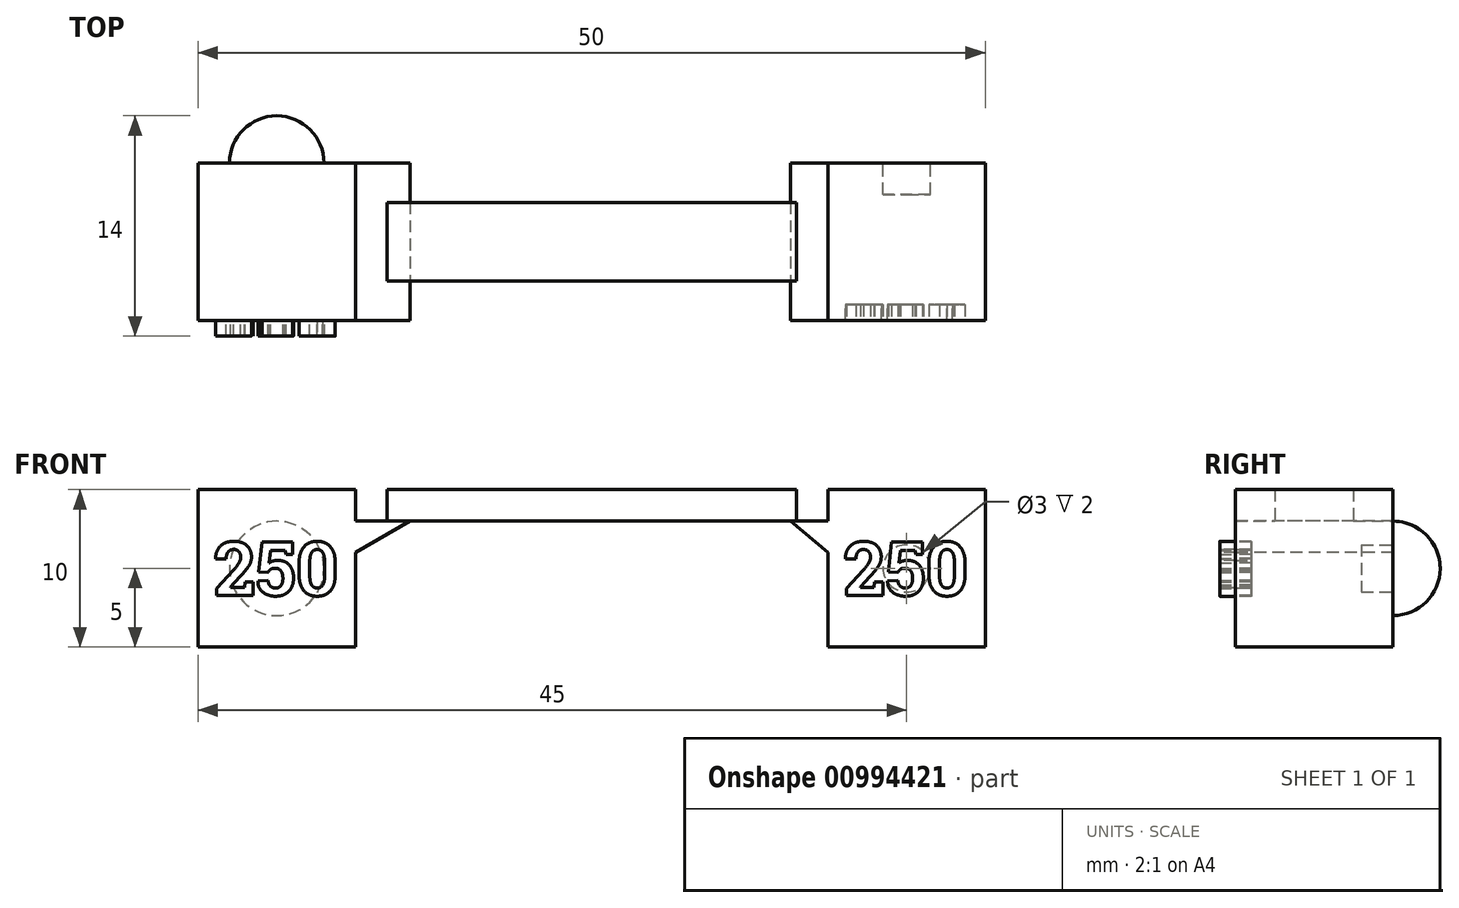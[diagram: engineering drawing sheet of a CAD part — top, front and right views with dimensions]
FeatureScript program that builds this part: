
annotation { "Feature Type Name" : "Feature", "Feature Type Description" : "" }
export const myFeature = defineFeature(function(context is Context, id is Id, definition is map)
    precondition{}
    {
        {
            var Q0;
            Q0=qCreatedBy(makeId("Top.planeOp"),FACE);
            var sketch = newSketch(context, id + "F0", { "sketchPlane" : qUnion([Q0])});
            skLineSegment(sketch, "E0.bottom", {"start": v(30, 10) * mm, "end": v(-30, 10) * mm});
            skLineSegment(sketch, "E0.top", {"start": v(30, -10) * mm, "end": v(-30, -10) * mm});
            skLineSegment(sketch, "E0.left", {"start": v(30, 10) * mm, "end": v(30, -10) * mm});
            skLineSegment(sketch, "E0.right", {"start": v(-30, 10) * mm, "end": v(-30, -10) * mm});
            skPoint(sketch, "E0.middle", {"position": v(0, 0) * mm});
            skLineSegment(sketch, "E1", {"start": v(0, 0) * mm, "end": v(-20, 0) * mm, "construction": true});
            skLineSegment(sketch, "E2.bottom", {"start": v(-15, 5) * mm, "end": v(-25, 5) * mm});
            skLineSegment(sketch, "E2.top", {"start": v(-15, -5) * mm, "end": v(-25, -5) * mm});
            skLineSegment(sketch, "E2.left", {"start": v(-15, 5) * mm, "end": v(-15, -5) * mm});
            skLineSegment(sketch, "E2.right", {"start": v(-25, 5) * mm, "end": v(-25, -5) * mm});
            skPoint(sketch, "E2.middle", {"position": v(-20, 0) * mm});
            skLineSegment(sketch, "E3", {"start": v(0, 0) * mm, "end": v(0, 4.45) * mm, "construction": true});
            skLineSegment(sketch, "E4.0", {"start": v(-16, 4) * mm, "end": v(-24, 4) * mm});
            skLineSegment(sketch, "E4.1", {"start": v(-16, 4) * mm, "end": v(-16, -4) * mm});
            skLineSegment(sketch, "E4.2", {"start": v(-16, -4) * mm, "end": v(-24, -4) * mm});
            skLineSegment(sketch, "E4.3", {"start": v(-24, 4) * mm, "end": v(-24, -4) * mm});
            skLineSegment(sketch, "E5.MirrorCS", {"start": v(-16, -4) * mm, "end": v(-16, 4) * mm});
            skLineSegment(sketch, "E6.MirrorCS", {"start": v(-25, -5) * mm, "end": v(-25, 5) * mm});
            skLineSegment(sketch, "E7.MirrorCS", {"start": v(-15, -5) * mm, "end": v(-15, 5) * mm});
            skLineSegment(sketch, "E8.MirrorCS", {"start": v(-24, -4) * mm, "end": v(-24, 4) * mm});
            skPoint(sketch, "E9.MirrorP", {"position": v(20, 0) * mm});
            skLineSegment(sketch, "E10.MirrorCS", {"start": v(25, 5) * mm, "end": v(25, -5) * mm});
            skLineSegment(sketch, "E11.MirrorCS", {"start": v(16, -4) * mm, "end": v(16, 4) * mm});
            skLineSegment(sketch, "E12.MirrorCS", {"start": v(15, -5) * mm, "end": v(25, -5) * mm});
            skLineSegment(sketch, "E13.MirrorCS", {"start": v(15, 5) * mm, "end": v(15, -5) * mm});
            skLineSegment(sketch, "E14.MirrorCS", {"start": v(16, -4) * mm, "end": v(24, -4) * mm});
            skLineSegment(sketch, "E15.MirrorCS", {"start": v(24, -4) * mm, "end": v(24, 4) * mm});
            skLineSegment(sketch, "E16.MirrorCS", {"start": v(15, 5) * mm, "end": v(25, 5) * mm});
            skLineSegment(sketch, "E17.MirrorCS", {"start": v(16, 4) * mm, "end": v(24, 4) * mm});
            skLineSegment(sketch, "E18.MirrorCS", {"start": v(16, 4) * mm, "end": v(16, -4) * mm});
            skLineSegment(sketch, "E19.MirrorCS", {"start": v(15, -5) * mm, "end": v(15, 5) * mm});
            skLineSegment(sketch, "E20.MirrorCS", {"start": v(24, 4) * mm, "end": v(24, -4) * mm});
            skLineSegment(sketch, "E21.MirrorCS", {"start": v(0, 0) * mm, "end": v(20, 0) * mm, "construction": true});
            skLineSegment(sketch, "E22.MirrorCS", {"start": v(25, -5) * mm, "end": v(25, 5) * mm});
            skLineSegment(sketch, "E23.bottom", {"start": v(15, 2.5) * mm, "end": v(-15, 2.5) * mm});
            skLineSegment(sketch, "E23.top", {"start": v(15, -2.5) * mm, "end": v(-15, -2.5) * mm});
            skLineSegment(sketch, "E23.left", {"start": v(15, 2.5) * mm, "end": v(15, -2.5) * mm});
            skLineSegment(sketch, "E23.right", {"start": v(-15, 2.5) * mm, "end": v(-15, -2.5) * mm});
            skSolve(sketch);
        }
        {
            var Q0;
            {var subQ4=sQuery(id+"F0.wireOp",EDGE,"E2.bottom");Q0=makeQuery(id+"F0.imprint","IMPRINT",FACE,{"disambiguationData":[TD([[makeQuery(id+"F0.imprint","IMPRINT",EDGE,{"derivedFrom":subQ4}),1.0]])]});}
            var Q1;
            Q1=makeQuery(id+"F0.imprint","IMPRINT",FACE,{"disambiguationData":[TD([[makeQuery(id+"F0.imprint","IMPRINT",EDGE,{"derivedFrom":sQuery(id+"F0.wireOp",EDGE,"E4.0")}),1.0]])]});
            var Q2;
            Q2=makeQuery(id+"F0.imprint","IMPRINT",FACE,{"disambiguationData":[TD([[makeQuery(id+"F0.imprint","IMPRINT",EDGE,{"derivedFrom":sQuery(id+"F0.wireOp",EDGE,"E11.MirrorCS")}),-1.0]])]});
            var Q3;
            Q3=makeQuery(id+"F0.imprint","IMPRINT",FACE,{"disambiguationData":[TD([[makeQuery(id+"F0.imprint","IMPRINT",EDGE,{"derivedFrom":sQuery(id+"F0.wireOp",EDGE,"E10.MirrorCS")}),-1.0]])]});
            var Q4;
            {var subQ0=sQuery(id+"F0.wireOp",EDGE,"E23.bottom");Q4=makeQuery(id+"F0.imprint","IMPRINT",FACE,{"disambiguationData":[TD([[makeQuery(id+"F0.imprint","IMPRINT",EDGE,{"derivedFrom":subQ0}),1.0]])]});}
            extrude(context, id + "F1", {"entities" : qUnion([Q0, Q1, Q2, Q3, Q4]), "depth" : 12 * mm, "offsetDistance" : 25 * mm, "hasSecondDirection" : true, "secondDirectionOppositeDirection" : false, "secondDirectionDepth" : 2 * mm});
        }
        {
            var Q0;
            Q0=makeQuery(id+"F1.opExtrude","SWEPT_FACE",FACE,{"disambiguationData":[OSD([sQuery(id+"F0.wireOp",EDGE,"E23.top")])]});
            var sketch = newSketch(context, id + "F2", { "sketchPlane" : qUnion([Q0])});
            skLineSegment(sketch, "E24.bottom", {"start": v(-15, 2) * mm, "end": v(15, 2) * mm});
            skLineSegment(sketch, "E24.top", {"start": v(-15, 8) * mm, "end": v(15, 8) * mm});
            skLineSegment(sketch, "E24.left", {"start": v(-15, 2) * mm, "end": v(-15, 8) * mm});
            skLineSegment(sketch, "E24.right", {"start": v(15, 2) * mm, "end": v(15, 8) * mm});
            skLineSegment(sketch, "E25.bottom", {"start": v(-13, 12) * mm, "end": v(13, 12) * mm});
            skLineSegment(sketch, "E25.top", {"start": v(-13, 10) * mm, "end": v(13, 10) * mm});
            skLineSegment(sketch, "E25.left", {"start": v(-13, 12) * mm, "end": v(-13, 10) * mm});
            skLineSegment(sketch, "E25.right", {"start": v(13, 12) * mm, "end": v(13, 10) * mm});
            skLineSegment(sketch, "E26", {"start": v(-15, 8) * mm, "end": v(-11.54, 10) * mm});
            skLineSegment(sketch, "E27", {"start": v(-11.54, 10) * mm, "end": v(-15, 10) * mm});
            skLineSegment(sketch, "E28", {"start": v(-15, 10) * mm, "end": v(-15, 8) * mm});
            skLineSegment(sketch, "E29", {"start": v(15, 8) * mm, "end": v(12.62, 10) * mm});
            skLineSegment(sketch, "E30", {"start": v(12.62, 10) * mm, "end": v(15, 10) * mm});
            skLineSegment(sketch, "E31", {"start": v(15, 10) * mm, "end": v(15, 8) * mm});
            skSolve(sketch);
        }
        {
            var Q0;
            Q0=makeQuery(id+"F2.imprint","IMPRINT",FACE,{"disambiguationData":[TD([[makeQuery(id+"F2.imprint","IMPRINT",EDGE,{"derivedFrom":sQuery(id+"F2.wireOp",EDGE,"E24.bottom")}),-1.0]])]});
            var Q1;
            Q1=makeQuery(id+"F2.imprint","IMPRINT",FACE,{"disambiguationData":[TD([[makeQuery(id+"F2.imprint","IMPRINT",EDGE,{"derivedFrom":sQuery(id+"F2.wireOp",EDGE,"E24.top")}),1.0]])]});
            var Q2;
            {var subQ0=sQuery(id+"F2.wireOp",EDGE,"E25.left");Q2=makeQuery(id+"F2.imprint","IMPRINT",FACE,{"disambiguationData":[TD([[makeQuery(id+"F2.imprint","IMPRINT",EDGE,{"derivedFrom":subQ0}),-1.0]])]});}
            var Q3;
            {var subQ0=sQuery(id+"F2.wireOp",EDGE,"E25.right");Q3=makeQuery(id+"F2.imprint","IMPRINT",FACE,{"disambiguationData":[TD([[makeQuery(id+"F2.imprint","IMPRINT",EDGE,{"derivedFrom":subQ0}),1.0]])]});}
            extrude(context, id + "F3", {"entities" : qUnion([Q0, Q1, Q2, Q3]), "operationType" : NewBodyOperationType.REMOVE, "oppositeDirection" : true, "depth" : 25 * mm, "offsetDistance" : 25 * mm});
        }
        {
            var Q0;
            {var subQ0=sQuery(id+"F2.wireOp",EDGE,"E26");Q0=makeQuery(id+"F2.imprint","IMPRINT",FACE,{"disambiguationData":[TD([[makeQuery(id+"F2.imprint","IMPRINT",EDGE,{"derivedFrom":subQ0}),1.0]])]});}
            var Q1;
            {var subQ0=sQuery(id+"F2.wireOp",EDGE,"E29");Q1=makeQuery(id+"F2.imprint","IMPRINT",FACE,{"disambiguationData":[TD([[makeQuery(id+"F2.imprint","IMPRINT",EDGE,{"derivedFrom":subQ0}),-1.0]])]});}
            extrude(context, id + "F4", {"entities" : qUnion([Q0, Q1]), "operationType" : NewBodyOperationType.ADD, "depth" : 2.5 * mm, "offsetDistance" : 25 * mm, "hasSecondDirection" : true, "secondDirectionOppositeDirection" : true, "secondDirectionDepth" : 7.5 * mm});
        }
        {
            var Q0;
            Q0=makeQuery(id+"F4.boolean.opBoolean","MERGE",FACE,{"derivedFrom":[makeQuery(id+"F1.opExtrude","SWEPT_FACE",FACE,{"disambiguationData":[OSD([sQuery(id+"F0.wireOp",EDGE,"E2.top")])]}),makeQuery(id+"F4.opExtrude","CAP_FACE",FACE,{"disambiguationData":[OSD([sQuery(id+"F2.wireOp",EDGE,"E26"),sQuery(id+"F2.wireOp",EDGE,"E27"),sQuery(id+"F2.wireOp",EDGE,"E28")])],"isStart":false})]});
            var sketch = newSketch(context, id + "F5", { "sketchPlane" : qUnion([Q0])});
            skText(sketch, "E32", { "text": "250", "fontName": "RobotoSlab-Bold.ttf"});
            skLineSegment(sketch, "E33", {"start": v(-25, 12) * mm, "end": v(-15, 2) * mm, "construction": true});
            skPoint(sketch, "E34", {"position": v(-20, 7) * mm});
            const initialGuessF5  = {"E32": [-0.024, 0.00528, 1, 0, 0.00344]};
            skSetInitialGuess(sketch, initialGuessF5);
            skSolve(sketch);
        }
        {
            var Q0;
            Q0=makeQuery(id+"F4.boolean.opBoolean","MERGE",FACE,{"derivedFrom":[makeQuery(id+"F1.opExtrude","SWEPT_FACE",FACE,{"disambiguationData":[OSD([sQuery(id+"F0.wireOp",EDGE,"E12.MirrorCS")])]}),makeQuery(id+"F4.opExtrude","CAP_FACE",FACE,{"disambiguationData":[OSD([sQuery(id+"F2.wireOp",EDGE,"E29"),sQuery(id+"F2.wireOp",EDGE,"E30"),sQuery(id+"F2.wireOp",EDGE,"E31")])],"isStart":false})]});
            var sketch = newSketch(context, id + "F6", { "sketchPlane" : qUnion([Q0])});
            skLineSegment(sketch, "E35", {"start": v(15, 12) * mm, "end": v(25, 2) * mm, "construction": true});
            skPoint(sketch, "E36", {"position": v(20, 7) * mm});
            skText(sketch, "E37", { "text": "250", "fontName": "RobotoSlab-Bold.ttf"});
            const initialGuessF6  = {"E37": [0.016, 0.00528, 1, 0, 0.00344]};
            skSetInitialGuess(sketch, initialGuessF6);
            skSolve(sketch);
        }
        {
            var Q0;
            Q0=qSketchRegion(id+"F5",true);
            extrude(context, id + "F7", {"entities" : qUnion([Q0]), "operationType" : NewBodyOperationType.ADD, "depth" : 1 * mm, "offsetDistance" : 25 * mm});
        }
        {
            var Q0;
            Q0=qSketchRegion(id+"F6",true);
            extrude(context, id + "F8", {"entities" : qUnion([Q0]), "operationType" : NewBodyOperationType.REMOVE, "oppositeDirection" : true, "depth" : 1 * mm, "offsetDistance" : 25 * mm});
        }
        {
            var Q0;
            Q0=makeQuery(id+"F4.boolean.opBoolean","MERGE",FACE,{"derivedFrom":[makeQuery(id+"F1.opExtrude","SWEPT_FACE",FACE,{"disambiguationData":[OSD([sQuery(id+"F0.wireOp",EDGE,"E16.MirrorCS")])]}),makeQuery(id+"F4.opExtrude","CAP_FACE",FACE,{"disambiguationData":[OSD([sQuery(id+"F2.wireOp",EDGE,"E29"),sQuery(id+"F2.wireOp",EDGE,"E30"),sQuery(id+"F2.wireOp",EDGE,"E31")])],"isStart":true})]});
            var sketch = newSketch(context, id + "F9", { "sketchPlane" : qUnion([Q0])});
            skLineSegment(sketch, "E38", {"start": v(-15, 12) * mm, "end": v(-25, 2) * mm, "construction": true});
            skPoint(sketch, "E39", {"position": v(-20, 7) * mm});
            skCircle(sketch, "E40", {"center": v(-20, 7) * mm, "radius": 1.5 * mm});
            skSolve(sketch);
        }
        {
            var Q0;
            Q0=makeQuery(id+"F4.boolean.opBoolean","MERGE",FACE,{"derivedFrom":[makeQuery(id+"F1.opExtrude","SWEPT_FACE",FACE,{"disambiguationData":[OSD([sQuery(id+"F0.wireOp",EDGE,"E2.bottom")])]}),makeQuery(id+"F4.opExtrude","CAP_FACE",FACE,{"disambiguationData":[OSD([sQuery(id+"F2.wireOp",EDGE,"E26"),sQuery(id+"F2.wireOp",EDGE,"E27"),sQuery(id+"F2.wireOp",EDGE,"E28")])],"isStart":true})]});
            var sketch = newSketch(context, id + "F10", { "sketchPlane" : qUnion([Q0])});
            skLineSegment(sketch, "E41", {"start": v(15, 12) * mm, "end": v(25, 2) * mm, "construction": true});
            skPoint(sketch, "E42", {"position": v(20, 7) * mm});
            skCircle(sketch, "E43", {"center": v(20, 7) * mm, "radius": 3 * mm});
            skSolve(sketch);
        }
        {
            var Q0;
            Q0=makeQuery(id+"F9.imprint","IMPRINT",FACE,{"disambiguationData":[TD([[makeQuery(id+"F9.imprint","IMPRINT",EDGE,{"derivedFrom":sQuery(id+"F9.wireOp",EDGE,"E40")}),1.0]])]});
            extrude(context, id + "F11", {"entities" : qUnion([Q0]), "operationType" : NewBodyOperationType.REMOVE, "oppositeDirection" : true, "depth" : 2 * mm, "offsetDistance" : 25 * mm});
        }
        {
            var Q0;
            Q0=makeQuery(id+"F10.imprint","IMPRINT",FACE,{"disambiguationData":[TD([[makeQuery(id+"F10.imprint","IMPRINT",EDGE,{"derivedFrom":sQuery(id+"F10.wireOp",EDGE,"E43")}),1.0]])]});
            extrude(context, id + "F12", {"entities" : qUnion([Q0]), "operationType" : NewBodyOperationType.ADD, "depth" : 3 * mm, "offsetDistance" : 25 * mm});
        }
        {
            var Q0;
            Q0=makeQuery(id+"F12.opExtrude","CAP_EDGE",EDGE,{"disambiguationData":[OSD([sQuery(id+"F10.wireOp",EDGE,"E43")])],"isStart":false});
            fillet(context, id + "F13", {"entities" : qUnion([Q0]), "radius" : 3 * mm, "tangentPropagation" : true, "allowEdgeOverflow" : false});
        }
    });
